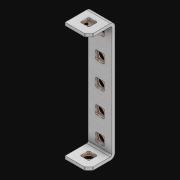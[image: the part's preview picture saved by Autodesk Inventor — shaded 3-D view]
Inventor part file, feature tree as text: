
AUTODESK INVENTOR PART (.ipt)
format: ipt  version: 2021 (Build 250183000, 183)  size: 2,735,104 bytes
history: native  units: in
note: dims shown in document units (in); Inventor stores cm internally (conversion verified against a paired STEP export)
features: extrude x8, other x7, sketch x4, thicken_offset x3, pattern_linear x3, imported_body x1
ambient origin geometry x8: Origin, YZ Plane, XZ Plane, XY Plane, X Axis, Y Axis, Z Axis, Center Point
bodies: Solid1 (feature_tree)
feature tree (26):
  thicken_offset  "Thicken1"
  thicken_offset  "Thicken2"
  thicken_offset  "Thicken3"
  pattern_linear  "Rectangular Pattern1"  Spacing1=0.001in  [1 undecoded]
  pattern_linear  "Rectangular Pattern2"  Spacing1=0.001in  [1 undecoded]
  pattern_linear  "Rectangular Pattern3"  Spacing1=0.182in  [1 undecoded]
  extrude  "Extrusion1"  Depth=0.063in TaperAngle=0.0deg
  sketch  "Sketch1"  dims[d0=0.001in]
  other  "Srf1"
  sketch  "Sketch2"  dims[d1=0.001in]
  other  "Srf2"
  sketch  "Sketch3"  dims[d2=0.001in]
  other  "Srf3"
  other  "Srf106"
  other  "Srf141"
  other  "Srf176"
  other  "Srf211"
  sketch  "Sketch4"  dims[d3=0.001in d4=0.001in d5=0.001in d6=0.182in d7=0.063in d8=0.0in d9=0.182in d10=0.063in d11=0.0in d12=0.182in d13=0.063in d14=0.0in d17=0.5in d18=0.3937in d20=0.5in d21=0.3937in d23=0.5in d24=1.9685in d26=0.5in d27=17.0in d28=0.0in]
  imported_body  "Imported1"
  extrude  "ExtrusionSrf1"  Depth=0.182in
  extrude  "ExtrusionSrf2"  Depth=0.063in TaperAngle=0.0deg
  extrude  "ExtrusionSrf3"  Depth=0.182in
  extrude  "ExtrusionSrf106"  Depth=0.063in TaperAngle=0.0deg
  extrude  "ExtrusionSrf141"  Depth=0.5in
  extrude  "ExtrusionSrf176"  Depth=0.3937in
  extrude  "ExtrusionSrf211"  Depth=0.5in
note: 3 required parameter values undecoded (feature->parameter linkage not recoverable at this tier; creation-order binding heuristic only, values carry confidence <= 0.55)
